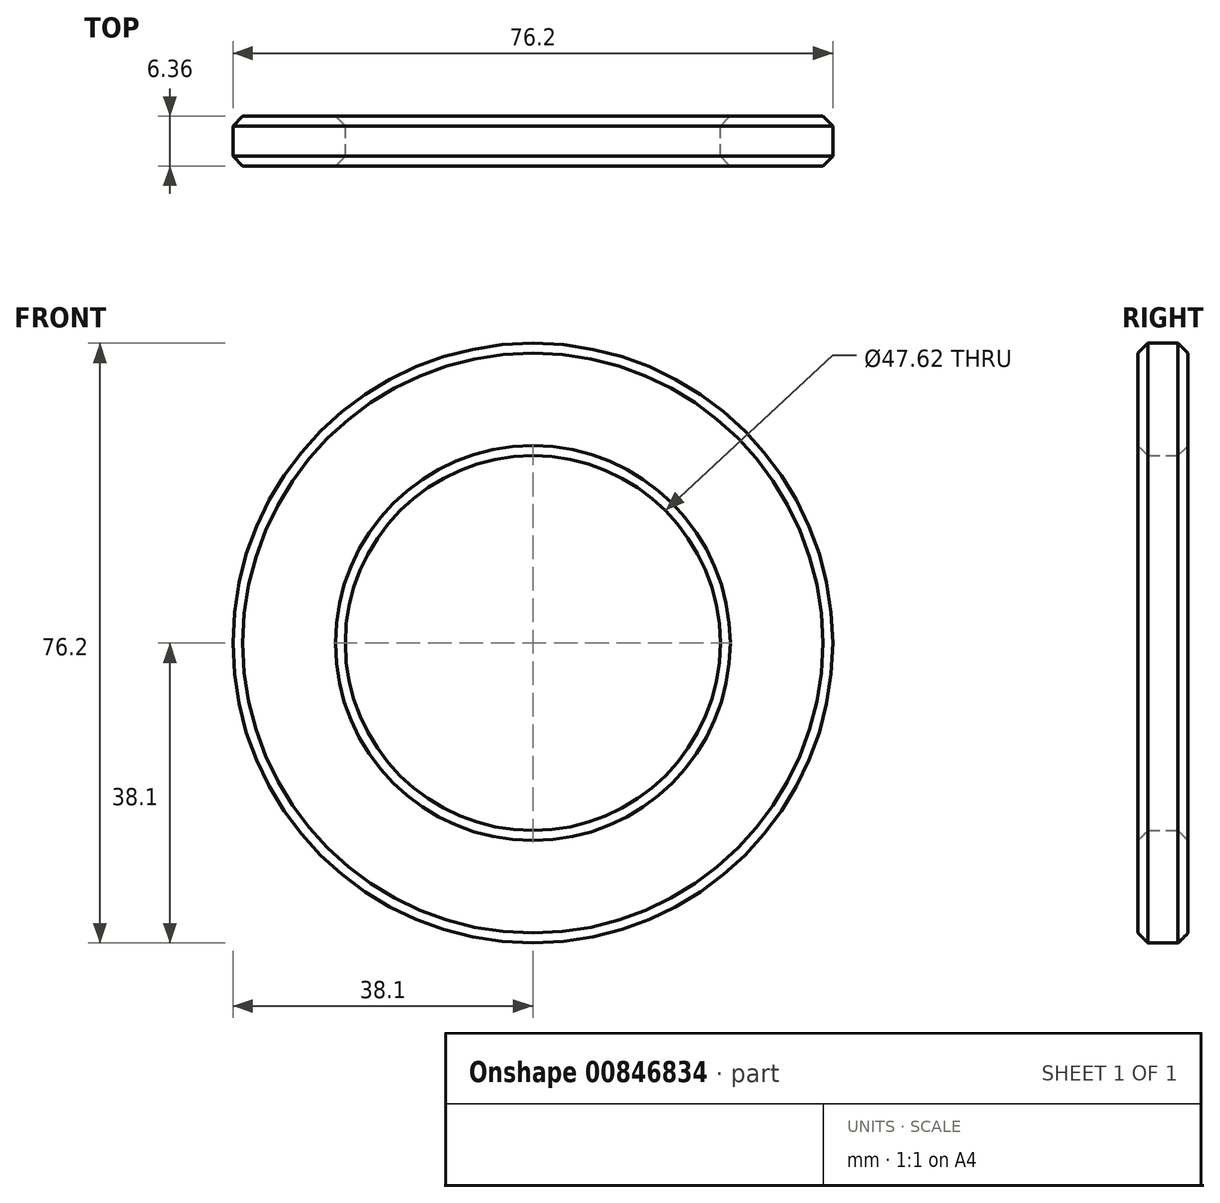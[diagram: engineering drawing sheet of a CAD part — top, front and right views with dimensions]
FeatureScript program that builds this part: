
annotation { "Feature Type Name" : "Feature", "Feature Type Description" : "" }
export const myFeature = defineFeature(function(context is Context, id is Id, definition is map)
    precondition{}
    {
        {
            var Q0;
            Q0=qCreatedBy(makeId("Front.planeOp"),FACE);
            var sketch = newSketch(context, id + "F0", { "sketchPlane" : qUnion([Q0])});
            skCircle(sketch, "E0", {"center": v(0, 0) * mm, "radius": 38.1 * mm});
            skCircle(sketch, "E1", {"center": v(0, 0) * mm, "radius": 23.81 * mm});
            skSolve(sketch);
        }
        {
            var Q0;
            Q0 = qSketchRegion(id + "F0", true);
            extrude(context, id + "F1", {"entities" : qUnion([Q0]), "depth" : 6.35 * mm, "offsetDistance" : 25.4 * mm, "symmetric" : true});
        }
        {
            var Q0;
            Q0=makeQuery(id+"F1.opExtrude","SWEPT_FACE",FACE,{"disambiguationData":[OSD([sQuery(id+"F0.wireOp",EDGE,"E0")])]});
            var Q1;
            Q1=makeQuery(id+"F1.opExtrude","SWEPT_FACE",FACE,{"disambiguationData":[OSD([sQuery(id+"F0.wireOp",EDGE,"E1")])]});
            chamfer(context, id + "F2", {"entities" : qUnion([Q0, Q1]), "width" : 1.27 * mm, "tangentPropagation" : true});
        }
    });
